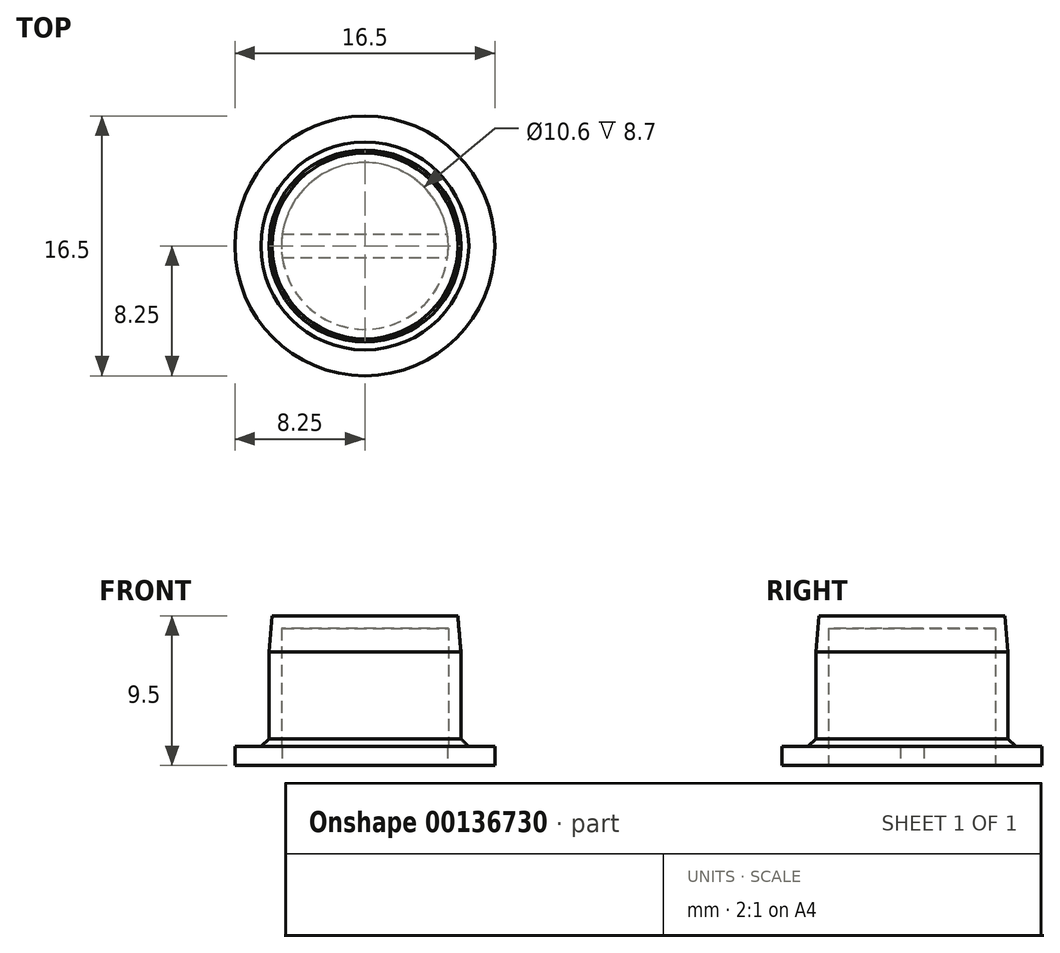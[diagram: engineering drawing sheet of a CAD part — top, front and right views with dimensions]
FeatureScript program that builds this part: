
annotation { "Feature Type Name" : "Feature", "Feature Type Description" : "" }
export const myFeature = defineFeature(function(context is Context, id is Id, definition is map)
    precondition{}
    {
        {
            var Q0;
            Q0=qCreatedBy(makeId("Top.planeOp"),FACE);
            var sketch = newSketch(context, id + "F0", { "sketchPlane" : qUnion([Q0])});
            skCircle(sketch, "E0", {"center": v(0, 0) * mm, "radius": 8.25 * mm});
            skCircle(sketch, "E1", {"center": v(0, 0) * mm, "radius": 6.1 * mm});
            skLineSegment(sketch, "E2.bottom", {"start": v(-7.5, -0.75) * mm, "end": v(7.5, -0.75) * mm});
            skLineSegment(sketch, "E2.top", {"start": v(-7.5, 0.75) * mm, "end": v(7.5, 0.75) * mm});
            skLineSegment(sketch, "E2.left", {"start": v(-7.5, -0.75) * mm, "end": v(-7.5, 0.75) * mm});
            skLineSegment(sketch, "E2.right", {"start": v(7.5, -0.75) * mm, "end": v(7.5, 0.75) * mm});
            skSolve(sketch);
        }
        {
            var Q0;
            {var subQ0=sQuery(id+"F0.wireOp",EDGE,"E2.top");var subQ1=sQuery(id+"F0.wireOp",EDGE,"E1");var subQ2=makeQuery(id+"F0.imprint","INTERSECT",VERTEX,{"disambiguationData":[OD(0.0)],"derivedFrom":[subQ1,subQ0]});Q0=makeQuery(id+"F0.imprint","IMPRINT",FACE,{"disambiguationData":[TD([[makeQuery(id+"F0.imprint","IMPRINT",EDGE,{"disambiguationData":[TD([[subQ2,1.0]])],"derivedFrom":subQ1}),1.0]])]});}
            var Q1;
            {var subQ0=sQuery(id+"F0.wireOp",EDGE,"E2.top");var subQ1=sQuery(id+"F0.wireOp",EDGE,"E1");var subQ2=makeQuery(id+"F0.imprint","INTERSECT",VERTEX,{"disambiguationData":[OD(0.0)],"derivedFrom":[subQ1,subQ0]});Q1=makeQuery(id+"F0.imprint","IMPRINT",FACE,{"disambiguationData":[TD([[makeQuery(id+"F0.imprint","IMPRINT",EDGE,{"disambiguationData":[TD([[subQ2,-1.0]])],"derivedFrom":subQ1}),1.0]])]});}
            var Q2;
            {var subQ0=sQuery(id+"F0.wireOp",EDGE,"E2.bottom");var subQ1=sQuery(id+"F0.wireOp",EDGE,"E1");var subQ2=makeQuery(id+"F0.imprint","INTERSECT",VERTEX,{"disambiguationData":[OD(0.0)],"derivedFrom":[subQ1,subQ0]});Q2=makeQuery(id+"F0.imprint","IMPRINT",FACE,{"disambiguationData":[TD([[makeQuery(id+"F0.imprint","IMPRINT",EDGE,{"disambiguationData":[TD([[subQ2,-1.0]])],"derivedFrom":subQ1}),1.0]])]});}
            extrude(context, id + "F1", {"entities" : qUnion([Q0, Q1, Q2]), "depth" : 9.5 * mm});
        }
        {
            var Q0;
            Q0=makeQuery(id+"F1.opExtrude","CAP_FACE",FACE,{"disambiguationData":[OSD([sQuery(id+"F0.wireOp",EDGE,"E1")])],"isStart":true});
            shell(context, id + "F2", {"entities" : qUnion([Q0]), "thickness" : 0.8 * mm});
        }
        {
            var Q0;
            Q0=makeQuery(id+"F0.imprint","IMPRINT",FACE,{"disambiguationData":[TD([[makeQuery(id+"F0.imprint","IMPRINT",EDGE,{"derivedFrom":sQuery(id+"F0.wireOp",EDGE,"E0")}),1.0]])]});
            var Q1;
            {var subQ0=sQuery(id+"F0.wireOp",EDGE,"E2.top");var subQ1=sQuery(id+"F0.wireOp",EDGE,"E1");var subQ2=makeQuery(id+"F0.imprint","INTERSECT",VERTEX,{"disambiguationData":[OD(0.0)],"derivedFrom":[subQ1,subQ0]});Q1=makeQuery(id+"F0.imprint","IMPRINT",FACE,{"disambiguationData":[TD([[makeQuery(id+"F0.imprint","IMPRINT",EDGE,{"disambiguationData":[TD([[subQ2,-1.0]])],"derivedFrom":subQ1}),1.0]])]});}
            var Q2;
            {var subQ5=sQuery(id+"F0.wireOp",EDGE,"E2.left");Q2=makeQuery(id+"F0.imprint","IMPRINT",FACE,{"disambiguationData":[TD([[makeQuery(id+"F0.imprint","IMPRINT",EDGE,{"derivedFrom":subQ5}),-1.0]])]});}
            var Q3;
            {var subQ5=sQuery(id+"F0.wireOp",EDGE,"E2.right");Q3=makeQuery(id+"F0.imprint","IMPRINT",FACE,{"disambiguationData":[TD([[makeQuery(id+"F0.imprint","IMPRINT",EDGE,{"derivedFrom":subQ5}),1.0]])]});}
            extrude(context, id + "F3", {"entities" : qUnion([Q0, Q1, Q2, Q3]), "operationType" : NewBodyOperationType.ADD, "depth" : 1.2 * mm});
        }
        {
            var Q0;
            Q0=makeQuery(id+"F1.opExtrude","CAP_EDGE",EDGE,{"disambiguationData":[OSD([sQuery(id+"F0.wireOp",EDGE,"E1")])],"isStart":false});
            chamfer(context, id + "F4", {"entities" : qUnion([Q0]), "chamferType" : ChamferType.OFFSET_ANGLE, "width" : 0.2 * mm, "oppositeDirection" : false, "angle" : 85 * degree, "tangentPropagation" : true});
        }
        {
            var Q0;
            Q0=makeQuery(id+"F3.opExtrude","CAP_EDGE",EDGE,{"disambiguationData":[OSD([sQuery(id+"F0.wireOp",EDGE,"E1")])],"isStart":false});
            chamfer(context, id + "F5", {"entities" : qUnion([Q0]), "width" : 0.5 * mm, "tangentPropagation" : true});
        }
    });
